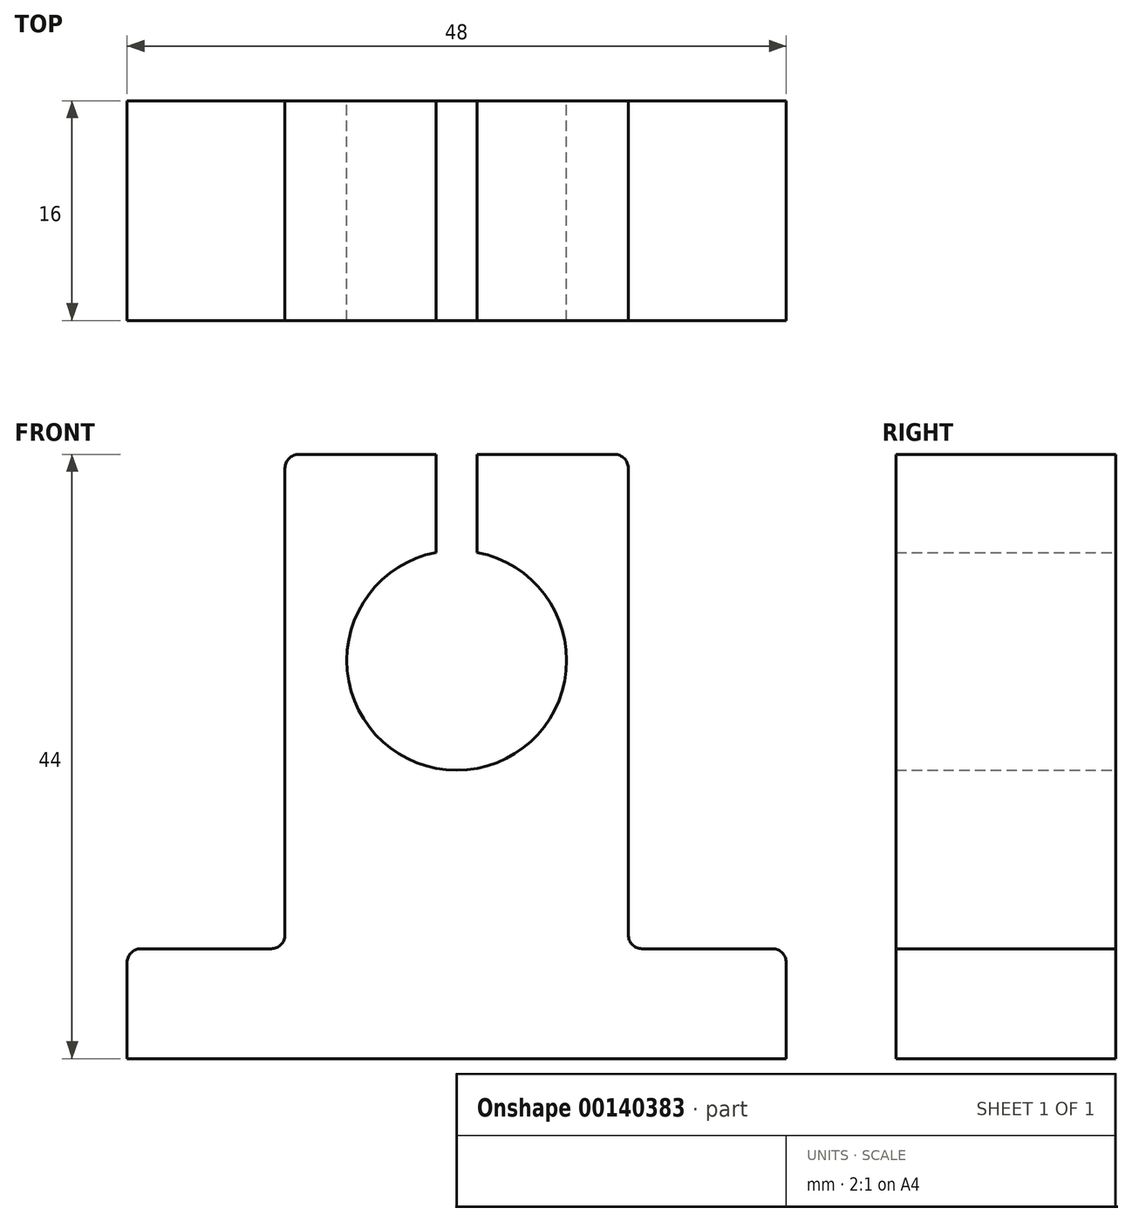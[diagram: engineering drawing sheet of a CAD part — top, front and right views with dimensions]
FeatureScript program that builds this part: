
annotation { "Feature Type Name" : "Feature", "Feature Type Description" : "" }
export const myFeature = defineFeature(function(context is Context, id is Id, definition is map)
    precondition{}
    {
        {
            var Q0;
            Q0=qCreatedBy(makeId("Front.planeOp"),FACE);
            var sketch = newSketch(context, id + "F0", { "sketchPlane" : qUnion([Q0])});
            skLineSegment(sketch, "E0", {"start": v(24, -29) * mm, "end": v(-24, -29) * mm});
            skLineSegment(sketch, "E1", {"start": v(-24, -29) * mm, "end": v(-24, -22) * mm});
            skLineSegment(sketch, "E2", {"start": v(-23, -21) * mm, "end": v(-13.5, -21) * mm});
            skLineSegment(sketch, "E3", {"start": v(-12.5, -20) * mm, "end": v(-12.5, 14) * mm});
            skLineSegment(sketch, "E4", {"start": v(-11.5, 15) * mm, "end": v(-1.5, 15) * mm});
            skLineSegment(sketch, "E5", {"start": v(12.5, 14) * mm, "end": v(12.5, -20) * mm});
            skLineSegment(sketch, "E6", {"start": v(13.5, -21) * mm, "end": v(23, -21) * mm});
            skLineSegment(sketch, "E7", {"start": v(24, -22) * mm, "end": v(24, -29) * mm});
            skLineSegment(sketch, "E8", {"start": v(0, 0) * mm, "end": v(0, 45.18) * mm, "construction": true});
            skLineSegment(sketch, "E9", {"start": v(0, 45.18) * mm, "end": v(0, -24.61) * mm, "construction": true});
            skPoint(sketch, "E10.visualSharp", {"position": v(-12.5, 15) * mm});
            skArc(sketch, "E10.filletArc", {"start": v(-11.5, 15) * mm, "mid": v(-12.2, 14.7) * mm, "end": v(-12.5, 14) * mm});
            skPoint(sketch, "E11.visualSharp", {"position": v(12.5, 15) * mm});
            skArc(sketch, "E11.filletArc", {"start": v(12.5, 14) * mm, "mid": v(12.2, 14.7) * mm, "end": v(11.5, 15) * mm});
            skPoint(sketch, "E12.visualSharp", {"position": v(12.5, -21) * mm});
            skArc(sketch, "E12.filletArc", {"start": v(12.5, -20) * mm, "mid": v(12.8, -20.7) * mm, "end": v(13.5, -21) * mm});
            skPoint(sketch, "E13.visualSharp", {"position": v(-12.5, -21) * mm});
            skArc(sketch, "E13.filletArc", {"start": v(-13.5, -21) * mm, "mid": v(-12.8, -20.7) * mm, "end": v(-12.5, -20) * mm});
            skArc(sketch, "E14", {"start": v(-1.5, 7.86) * mm, "mid": v(0, -8) * mm, "end": v(1.5, 7.86) * mm});
            skLineSegment(sketch, "E15", {"start": v(-1.5, 15) * mm, "end": v(-1.5, 7.86) * mm});
            skLineSegment(sketch, "E16.MirrorCS", {"start": v(1.5, 15) * mm, "end": v(1.5, 7.86) * mm});
            skPoint(sketch, "E17.orphan", {"position": v(1.5, 3.15) * mm});
            skPoint(sketch, "E18.orphan", {"position": v(-1.5, 3.15) * mm});
            skLineSegment(sketch, "E19.trimOffspring", {"start": v(1.5, 15) * mm, "end": v(11.5, 15) * mm});
            skPoint(sketch, "E20.orphan", {"position": v(-1.5, 21.4) * mm});
            skPoint(sketch, "E21.orphan", {"position": v(1.5, 21.4) * mm});
            skPoint(sketch, "E22.visualSharp", {"position": v(24, -21) * mm});
            skArc(sketch, "E22.filletArc", {"start": v(24, -22) * mm, "mid": v(23.7, -21.3) * mm, "end": v(23, -21) * mm});
            skPoint(sketch, "E23.visualSharp", {"position": v(-24, -21) * mm});
            skArc(sketch, "E23.filletArc", {"start": v(-23, -21) * mm, "mid": v(-23.7, -21.3) * mm, "end": v(-24, -22) * mm});
            skSolve(sketch);
        }
        {
            var Q0;
            Q0=makeQuery(id+"F0.imprint","IMPRINT",FACE,{"disambiguationData":[TD([[makeQuery(id+"F0.imprint","IMPRINT",EDGE,{"derivedFrom":sQuery(id+"F0.wireOp",EDGE,"E0")}),-1.0]])]});
            extrude(context, id + "F1", {"entities" : qUnion([Q0]), "endBound" : BoundingType.SYMMETRIC, "depth" : 16 * mm});
        }
    });
